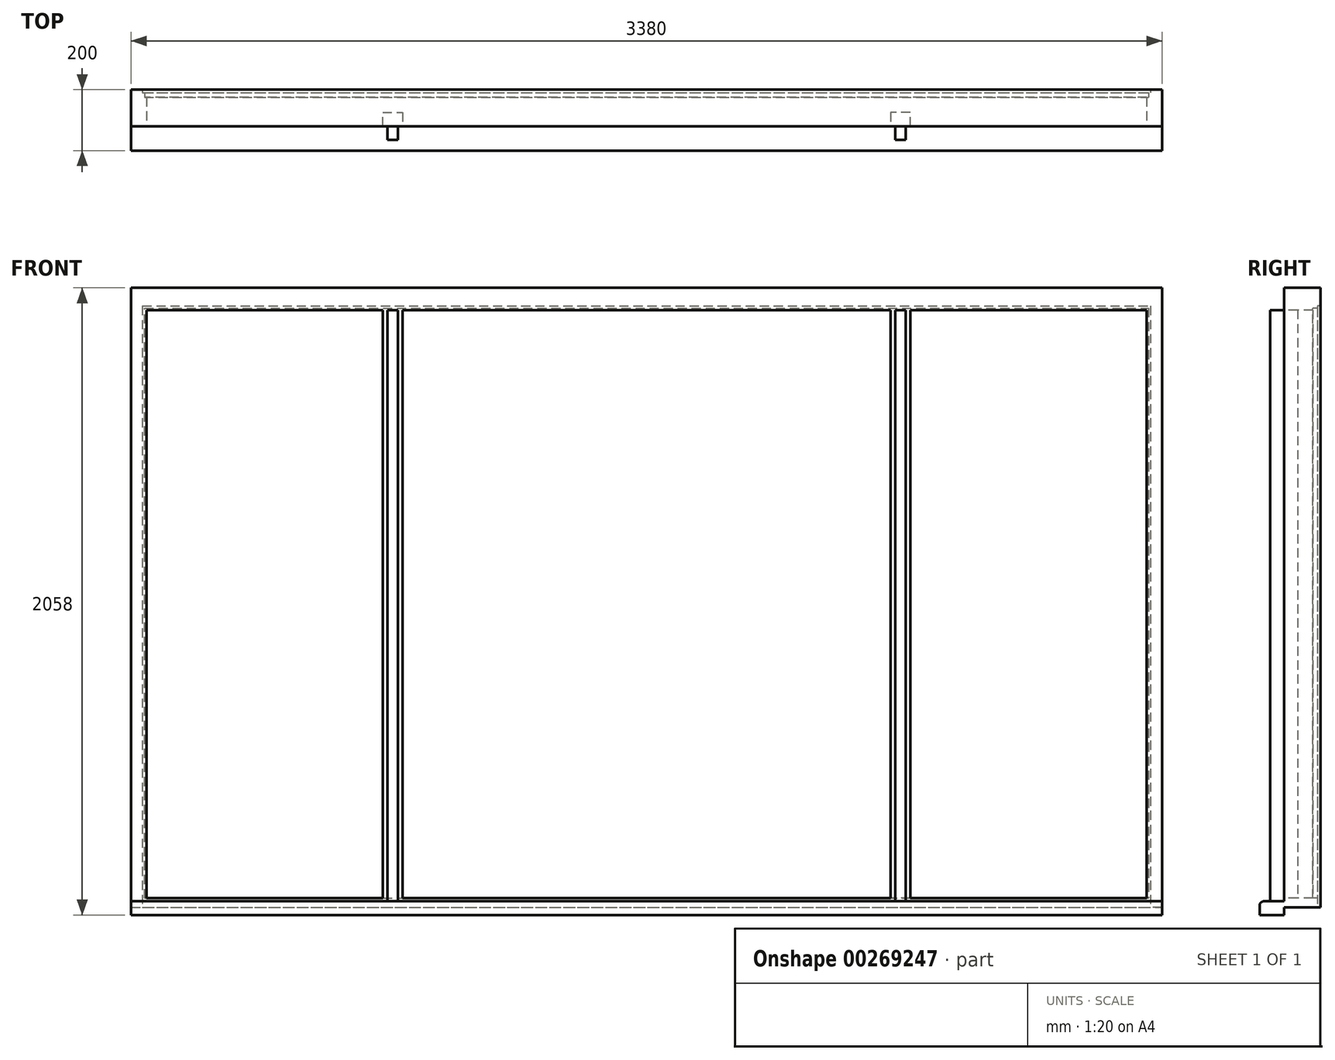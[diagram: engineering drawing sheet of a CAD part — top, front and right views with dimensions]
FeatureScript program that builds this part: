
annotation { "Feature Type Name" : "Feature", "Feature Type Description" : "" }
export const myFeature = defineFeature(function(context is Context, id is Id, definition is map)
    precondition{}
    {
        {
            var Q0;
            Q0=qCreatedBy(makeId("Top.planeOp"),FACE);
            var sketch = newSketch(context, id + "F0", { "sketchPlane" : qUnion([Q0])});
            skLineSegment(sketch, "E0", {"start": v(-800, 0) * mm, "end": v(-815, 0) * mm});
            skLineSegment(sketch, "E1", {"start": v(-815, 0) * mm, "end": v(-815, -45) * mm});
            skLineSegment(sketch, "E2", {"start": v(-815, -45) * mm, "end": v(-850, -45) * mm});
            skLineSegment(sketch, "E3", {"start": v(-850, -45) * mm, "end": v(-850, 0) * mm});
            skLineSegment(sketch, "E4", {"start": v(-850, 0) * mm, "end": v(-865, 0) * mm});
            skLineSegment(sketch, "E5", {"start": v(-865, 0) * mm, "end": v(-865, 45) * mm});
            skLineSegment(sketch, "E6", {"start": v(-865, 45) * mm, "end": v(-800, 45) * mm});
            skLineSegment(sketch, "E7", {"start": v(-800, 45) * mm, "end": v(-800, 0) * mm});
            skLineSegment(sketch, "E8.bottom", {"start": v(-1640, 0) * mm, "end": v(-1690, 0) * mm});
            skLineSegment(sketch, "E8.top", {"start": v(-1640, 95) * mm, "end": v(-1690, 95) * mm});
            skLineSegment(sketch, "E8.left", {"start": v(-1640, 95) * mm, "end": v(-1640, 0) * mm});
            skLineSegment(sketch, "E8.right", {"start": v(-1690, 95) * mm, "end": v(-1690, 0) * mm});
            skSolve(sketch);
        }
        {
            var Q0;
            Q0=makeQuery(id+"F0.imprint","IMPRINT",FACE,{"disambiguationData":[TD([[makeQuery(id+"F0.imprint","IMPRINT",EDGE,{"derivedFrom":sQuery(id+"F0.wireOp",EDGE,"E0")}),-1.0]])]});
            var Q1;
            Q1=makeQuery(id+"F0.imprint","IMPRINT",FACE,{"disambiguationData":[TD([[makeQuery(id+"F0.imprint","IMPRINT",EDGE,{"derivedFrom":sQuery(id+"F0.wireOp",EDGE,"E8.bottom")}),-1.0]])]});
            extrude(context, id + "F1", {"entities" : qUnion([Q0, Q1]), "depth" : 1930 * mm});
        }
        {
            var Q0;
            Q0=makeQuery(id+"F1.opExtrude","CAP_FACE",FACE,{"disambiguationData":[OSD([sQuery(id+"F0.wireOp",EDGE,"E0"),sQuery(id+"F0.wireOp",EDGE,"E1"),sQuery(id+"F0.wireOp",EDGE,"E2"),sQuery(id+"F0.wireOp",EDGE,"E3"),sQuery(id+"F0.wireOp",EDGE,"E4"),sQuery(id+"F0.wireOp",EDGE,"E5"),sQuery(id+"F0.wireOp",EDGE,"E6"),sQuery(id+"F0.wireOp",EDGE,"E7")])],"isStart":true});
            var sketch = newSketch(context, id + "F2", { "sketchPlane" : qUnion([Q0])});
            skLineSegment(sketch, "E9.bottom", {"start": v(-1690, 0) * mm, "end": v(0, 0) * mm});
            skLineSegment(sketch, "E9.top", {"start": v(-1690, -110) * mm, "end": v(0, -110) * mm});
            skLineSegment(sketch, "E9.left", {"start": v(-1690, 0) * mm, "end": v(-1690, -110) * mm});
            skLineSegment(sketch, "E9.right", {"start": v(0, 0) * mm, "end": v(0, -110) * mm});
            skSolve(sketch);
        }
        {
            var Q0;
            Q0 = qSketchRegion(id + "F2", true);
            extrude(context, id + "F3", {"entities" : qUnion([Q0]), "operationType" : NewBodyOperationType.ADD, "depth" : 30 * mm});
        }
        {
            var Q0;
            Q0=makeQuery(id+"F3.boolean.opBoolean","MERGE",FACE,{"derivedFrom":[makeQuery(id+"F1.opExtrude","SWEPT_FACE",FACE,{"disambiguationData":[OSD([sQuery(id+"F0.wireOp",EDGE,"E0")])]}),makeQuery(id+"F1.opExtrude","SWEPT_FACE",FACE,{"disambiguationData":[OSD([sQuery(id+"F0.wireOp",EDGE,"E4")])]}),makeQuery(id+"F1.opExtrude","SWEPT_FACE",FACE,{"disambiguationData":[OSD([sQuery(id+"F0.wireOp",EDGE,"E8.bottom")])]}),makeQuery(id+"F3.opExtrude","SWEPT_FACE",FACE,{"disambiguationData":[OSD([sQuery(id+"F2.wireOp",EDGE,"E9.bottom")])]})]});
            var sketch = newSketch(context, id + "F4", { "sketchPlane" : qUnion([Q0])});
            skLineSegment(sketch, "E10.bottom", {"start": v(0, -10) * mm, "end": v(-1690, -10) * mm});
            skLineSegment(sketch, "E10.top", {"start": v(0, -55) * mm, "end": v(-1690, -55) * mm});
            skLineSegment(sketch, "E10.left", {"start": v(0, -10) * mm, "end": v(0, -55) * mm});
            skLineSegment(sketch, "E10.right", {"start": v(-1690, -10) * mm, "end": v(-1690, -55) * mm});
            skSolve(sketch);
        }
        {
            var Q0;
            Q0 = qSketchRegion(id + "F4", true);
            extrude(context, id + "F5", {"entities" : qUnion([Q0]), "operationType" : NewBodyOperationType.ADD, "depth" : 80 * mm});
        }
        {
            var Q0;
            Q0 = qSketchRegion(id + "F0", true);
            extrude(context, id + "F6", {"entities" : qUnion([Q0]), "operationType" : NewBodyOperationType.ADD, "oppositeDirection" : true, "depth" : 25 * mm});
        }
        {
            var Q0;
            Q0=makeQuery(id+"F5.opExtrude","CAP_EDGE",EDGE,{"disambiguationData":[OSD([sQuery(id+"F4.wireOp",EDGE,"E10.bottom")])],"isStart":false});
            fillet(context, id + "F7", {"entities" : qUnion([Q0]), "radius" : 15 * mm, "tangentPropagation" : true, "allowEdgeOverflow" : false});
        }
        {
            var Q0;
            Q0=makeQuery(id+"F3.opExtrude","CAP_FACE",FACE,{"disambiguationData":[OSD([sQuery(id+"F2.wireOp",EDGE,"E9.bottom"),sQuery(id+"F2.wireOp",EDGE,"E9.top"),sQuery(id+"F2.wireOp",EDGE,"E9.left"),sQuery(id+"F2.wireOp",EDGE,"E9.right")])],"isStart":false});
            var sketch = newSketch(context, id + "F8", { "sketchPlane" : qUnion([Q0])});
            skLineSegment(sketch, "E11", {"start": v(-1690, -110) * mm, "end": v(-1690, -120) * mm});
            skLineSegment(sketch, "E12", {"start": v(-1690, -120) * mm, "end": v(-1653, -120) * mm});
            skLineSegment(sketch, "E13", {"start": v(-1653, -120) * mm, "end": v(-1653, -110) * mm});
            skLineSegment(sketch, "E14", {"start": v(-1653, -110) * mm, "end": v(-1646, -110) * mm});
            skLineSegment(sketch, "E15", {"start": v(-1646, -110) * mm, "end": v(-1646, -90) * mm});
            skLineSegment(sketch, "E16", {"start": v(-1646, -90) * mm, "end": v(-1690, -90) * mm});
            skLineSegment(sketch, "E17", {"start": v(-1690, -90) * mm, "end": v(-1690, -110) * mm});
            skSolve(sketch);
        }
        {
            var Q0;
            Q0 = qSketchRegion(id + "F8", true);
            var Q1;
            Q1=makeQuery(id+"F1.opExtrude","CAP_FACE",FACE,{"disambiguationData":[OSD([sQuery(id+"F0.wireOp",EDGE,"E8.bottom"),sQuery(id+"F0.wireOp",EDGE,"E8.top"),sQuery(id+"F0.wireOp",EDGE,"E8.left"),sQuery(id+"F0.wireOp",EDGE,"E8.right")])],"isStart":false});
            extrude(context, id + "F9", {"entities" : qUnion([Q0]), "operationType" : NewBodyOperationType.ADD, "oppositeDirection" : true, "endBoundEntityFace" : qUnion([Q1]), "depth" : 2033 * mm});
        }
        {
            var Q0;
            Q0=makeQuery(id+"F1.opExtrude","SWEPT_FACE",FACE,{"disambiguationData":[OSD([sQuery(id+"F0.wireOp",EDGE,"E8.left")])]});
            var sketch = newSketch(context, id + "F10", { "sketchPlane" : qUnion([Q0])});
            skLineSegment(sketch, "E18", {"start": v(0, 1930) * mm, "end": v(0, 2003) * mm});
            skLineSegment(sketch, "E19", {"start": v(0, 2003) * mm, "end": v(120, 2003) * mm});
            skLineSegment(sketch, "E20", {"start": v(120, 2003) * mm, "end": v(120, 1943) * mm});
            skLineSegment(sketch, "E21", {"start": v(120, 1943) * mm, "end": v(110, 1943) * mm});
            skLineSegment(sketch, "E22", {"start": v(110, 1943) * mm, "end": v(110, 1936.5) * mm});
            skLineSegment(sketch, "E23", {"start": v(110, 1936.5) * mm, "end": v(95, 1936.5) * mm});
            skLineSegment(sketch, "E24", {"start": v(95, 1936.5) * mm, "end": v(95, 1930) * mm});
            skLineSegment(sketch, "E25", {"start": v(95, 1930) * mm, "end": v(0, 1930) * mm});
            skSolve(sketch);
        }
        {
            var Q0;
            Q0=makeQuery(id+"F10.imprint","IMPRINT",FACE,{"disambiguationData":[TD([[makeQuery(id+"F10.imprint","IMPRINT",EDGE,{"derivedFrom":sQuery(id+"F10.wireOp",EDGE,"E18")}),-1.0]])]});
            var Q1;
            Q1=makeQuery(id+"F9.boolean.opBoolean","MERGE",FACE,{"derivedFrom":[makeQuery(id+"F3.boolean.opBoolean","MERGE",FACE,{"derivedFrom":[makeQuery(id+"F1.opExtrude","SWEPT_FACE",FACE,{"disambiguationData":[OSD([sQuery(id+"F0.wireOp",EDGE,"E8.right")])]}),makeQuery(id+"F3.opExtrude","SWEPT_FACE",FACE,{"disambiguationData":[OSD([sQuery(id+"F2.wireOp",EDGE,"E9.left")])]})]}),makeQuery(id+"F9.opExtrude","SWEPT_FACE",FACE,{"disambiguationData":[OSD([sQuery(id+"F8.wireOp",EDGE,"E11"),sQuery(id+"F8.wireOp",EDGE,"E17")])]})]});
            extrude(context, id + "F11", {"entities" : qUnion([Q0]), "operationType" : NewBodyOperationType.ADD, "endBound" : BoundingType.UP_TO_SURFACE, "oppositeDirection" : true, "endBoundEntityFace" : qUnion([Q1]), "depth" : 25 * mm});
        }
        {
            var Q0;
            Q0 = qSketchRegion(id + "F10", true);
            var Q1;
            Q1=makeQuery(id+"F5.boolean.opBoolean","MERGE",FACE,{"derivedFrom":[makeQuery(id+"F3.opExtrude","SWEPT_FACE",FACE,{"disambiguationData":[OSD([sQuery(id+"F2.wireOp",EDGE,"E9.right")])]}),makeQuery(id+"F5.opExtrude","SWEPT_FACE",FACE,{"disambiguationData":[OSD([sQuery(id+"F4.wireOp",EDGE,"E10.left")])]})]});
            extrude(context, id + "F12", {"entities" : qUnion([Q0]), "operationType" : NewBodyOperationType.ADD, "endBound" : BoundingType.UP_TO_SURFACE, "endBoundEntityFace" : qUnion([Q1]), "depth" : 402 * mm});
        }
        {
            var Q0;
            Q0=makeQuery(id+"F1.opExtrude","SWEPT_BODY",BODY,{"disambiguationData":[OSD([sQuery(id+"F0.wireOp",EDGE,"E0"),sQuery(id+"F0.wireOp",EDGE,"E1"),sQuery(id+"F0.wireOp",EDGE,"E2"),sQuery(id+"F0.wireOp",EDGE,"E3"),sQuery(id+"F0.wireOp",EDGE,"E4"),sQuery(id+"F0.wireOp",EDGE,"E5"),sQuery(id+"F0.wireOp",EDGE,"E6"),sQuery(id+"F0.wireOp",EDGE,"E7")])]});
            var Q1;
            Q1=qCreatedBy(makeId("Right.planeOp"),FACE);
            mirror(context, id + "F13", {"operationType" : NewBodyOperationType.ADD, "entities" : qUnion([Q0]), "mirrorPlane" : qUnion([Q1])});
        }
    });
